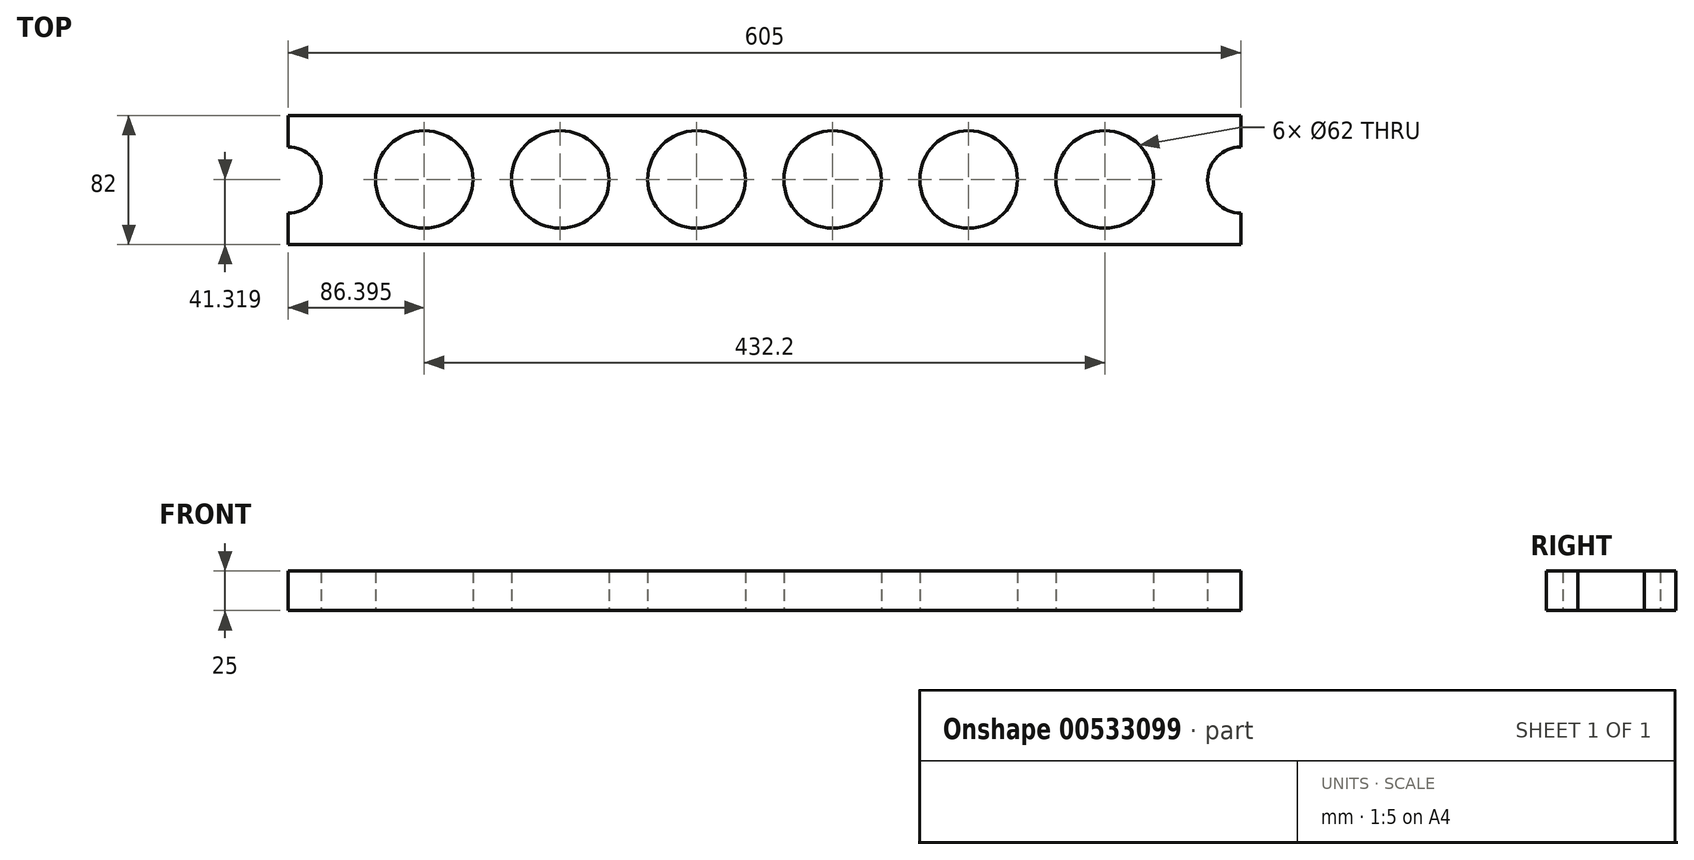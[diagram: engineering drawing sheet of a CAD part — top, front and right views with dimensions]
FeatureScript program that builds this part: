
annotation { "Feature Type Name" : "Feature", "Feature Type Description" : "" }
export const myFeature = defineFeature(function(context is Context, id is Id, definition is map)
    precondition{}
    {
        {
            var Q0;
            Q0=qCreatedBy(makeId("Top.planeOp"),FACE);
            var sketch = newSketch(context, id + "F0", { "sketchPlane" : qUnion([Q0])});
            skCircle(sketch, "E0", {"center": v(129.46, 164.36) * mm, "radius": 31 * mm});
            skCircle(sketch, "E1", {"center": v(43.06, 164.36) * mm, "radius": 31 * mm});
            skCircle(sketch, "E2", {"center": v(-43.34, 164.36) * mm, "radius": 31 * mm});
            skCircle(sketch, "E3", {"center": v(-129.94, 164.36) * mm, "radius": 31 * mm});
            skCircle(sketch, "E4", {"center": v(-216.34, 164.36) * mm, "radius": 31 * mm});
            skCircle(sketch, "E5", {"center": v(215.86, 164.36) * mm, "radius": 31 * mm});
            skLineSegment(sketch, "E6.top", {"start": v(-302.74, 123.04) * mm, "end": v(302.26, 123.04) * mm});
            skLineSegment(sketch, "E7", {"start": v(-302.74, 205.04) * mm, "end": v(302.26, 205.04) * mm});
            skCircle(sketch, "E8", {"center": v(-216.34, 164.36) * mm, "radius": 34 * mm, "construction": true});
            skLineSegment(sketch, "E9", {"start": v(-302.74, 205.04) * mm, "end": v(-302.74, 185.04) * mm});
            skLineSegment(sketch, "E10", {"start": v(-302.74, 143.04) * mm, "end": v(-302.74, 123.04) * mm});
            skArc(sketch, "E11", {"start": v(-302.74, 143.04) * mm, "mid": v(-281.74, 164.04) * mm, "end": v(-302.74, 185.04) * mm});
            skLineSegment(sketch, "E12", {"start": v(302.26, 205.04) * mm, "end": v(302.26, 185.04) * mm});
            skLineSegment(sketch, "E13", {"start": v(302.26, 123.04) * mm, "end": v(302.26, 143.04) * mm});
            skArc(sketch, "E14", {"start": v(302.26, 185.04) * mm, "mid": v(281.26, 164.04) * mm, "end": v(302.26, 143.04) * mm});
            skSolve(sketch);
        }
        {
            var Q0;
            Q0=makeQuery(id+"F0.imprint","IMPRINT",FACE,{"disambiguationData":[TD([[makeQuery(id+"F0.imprint","IMPRINT",EDGE,{"derivedFrom":sQuery(id+"F0.wireOp",EDGE,"E0")}),-1.0]])]});
            extrude(context, id + "F1", {"entities" : qUnion([Q0]), "depth" : 25 * mm});
        }
    });
